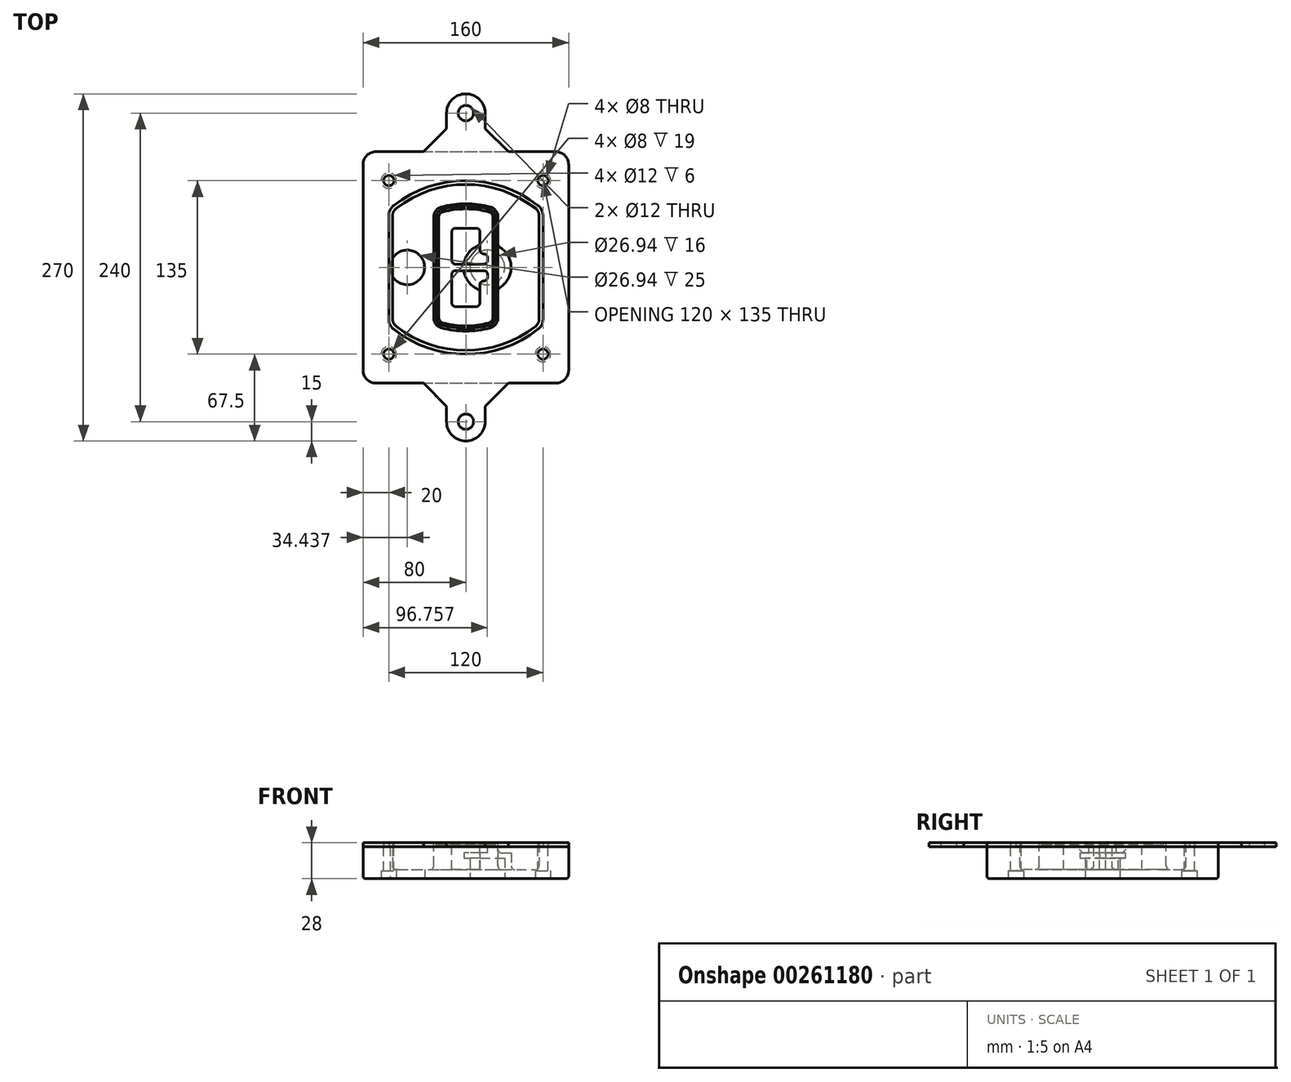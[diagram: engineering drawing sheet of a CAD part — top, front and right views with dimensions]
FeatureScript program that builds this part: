
annotation { "Feature Type Name" : "Feature", "Feature Type Description" : "" }
export const myFeature = defineFeature(function(context is Context, id is Id, definition is map)
    precondition{}
    {
        {
            var Q0;
            Q0=qCreatedBy(makeId("Top.planeOp"),FACE);
            var sketch = newSketch(context, id + "F0", { "sketchPlane" : qUnion([Q0])});
            skPoint(sketch, "E0.rect.middle", {"position": v(0, 0) * mm});
            skLineSegment(sketch, "E1.bottom", {"start": v(-70, -90) * mm, "end": v(70, -90) * mm});
            skLineSegment(sketch, "E1.top", {"start": v(-70, 90) * mm, "end": v(70, 90) * mm});
            skLineSegment(sketch, "E1.left", {"start": v(-80, -80) * mm, "end": v(-80, 80) * mm});
            skLineSegment(sketch, "E1.right", {"start": v(80, -80) * mm, "end": v(80, 80) * mm});
            skLineSegment(sketch, "E2", {"start": v(-80, 90) * mm, "end": v(80, -90) * mm, "construction": true});
            skLineSegment(sketch, "E3", {"start": v(80, 90) * mm, "end": v(-80, -90) * mm, "construction": true});
            skCircle(sketch, "E4", {"center": v(-60, 67.5) * mm, "radius": 4 * mm});
            skCircle(sketch, "E5", {"center": v(60, 67.5) * mm, "radius": 4 * mm});
            skCircle(sketch, "E6", {"center": v(60, -67.5) * mm, "radius": 4 * mm});
            skCircle(sketch, "E7", {"center": v(-60, -67.5) * mm, "radius": 4 * mm});
            skLineSegment(sketch, "E8", {"start": v(-60, 67.5) * mm, "end": v(60, 67.5) * mm, "construction": true});
            skLineSegment(sketch, "E9", {"start": v(60, 67.5) * mm, "end": v(60, -67.5) * mm, "construction": true});
            skLineSegment(sketch, "E10", {"start": v(60, -67.5) * mm, "end": v(-60, -67.5) * mm, "construction": true});
            skLineSegment(sketch, "E11", {"start": v(-60, -67.5) * mm, "end": v(-60, 67.5) * mm, "construction": true});
            skLineSegment(sketch, "E12", {"start": v(-60, 40.3) * mm, "end": v(-60, -40.3) * mm});
            skLineSegment(sketch, "E13", {"start": v(60, 40.3) * mm, "end": v(60, -40.3) * mm});
            skArc(sketch, "E14", {"start": v(56.15, 48.18) * mm, "mid": v(0, 67.5) * mm, "end": v(-56.15, 48.18) * mm});
            skArc(sketch, "E15", {"start": v(-56.15, -48.18) * mm, "mid": v(0, -67.5) * mm, "end": v(56.15, -48.18) * mm});
            skLineSegment(sketch, "E16", {"start": v(-60, 0) * mm, "end": v(60, 0) * mm, "construction": true});
            skPoint(sketch, "E17.visualSharp", {"position": v(-60, -45) * mm});
            skArc(sketch, "E17.filletArc", {"start": v(-60, -40.3) * mm, "mid": v(-58.99, -44.68) * mm, "end": v(-56.15, -48.18) * mm});
            skPoint(sketch, "E18.visualSharp", {"position": v(-60, 45) * mm});
            skArc(sketch, "E18.filletArc", {"start": v(-56.15, 48.18) * mm, "mid": v(-58.99, 44.68) * mm, "end": v(-60, 40.3) * mm});
            skPoint(sketch, "E19.visualSharp", {"position": v(60, 45) * mm});
            skArc(sketch, "E19.filletArc", {"start": v(60, 40.3) * mm, "mid": v(58.99, 44.68) * mm, "end": v(56.15, 48.18) * mm});
            skPoint(sketch, "E20.visualSharp", {"position": v(60, -45) * mm});
            skArc(sketch, "E20.filletArc", {"start": v(56.15, -48.18) * mm, "mid": v(58.99, -44.68) * mm, "end": v(60, -40.3) * mm});
            skPoint(sketch, "E21.visualSharp", {"position": v(-80, 90) * mm});
            skArc(sketch, "E21.filletArc", {"start": v(-70, 90) * mm, "mid": v(-77.07, 87.07) * mm, "end": v(-80, 80) * mm});
            skPoint(sketch, "E22.visualSharp", {"position": v(80, 90) * mm});
            skArc(sketch, "E22.filletArc", {"start": v(80, 80) * mm, "mid": v(77.07, 87.07) * mm, "end": v(70, 90) * mm});
            skPoint(sketch, "E23.visualSharp", {"position": v(80, -90) * mm});
            skArc(sketch, "E23.filletArc", {"start": v(70, -90) * mm, "mid": v(77.07, -87.07) * mm, "end": v(80, -80) * mm});
            skPoint(sketch, "E24.visualSharp", {"position": v(-80, -90) * mm});
            skArc(sketch, "E24.filletArc", {"start": v(-80, -80) * mm, "mid": v(-77.07, -87.07) * mm, "end": v(-70, -90) * mm});
            skArc(sketch, "E25.0", {"start": v(57, 40.3) * mm, "mid": v(56.3, 43.36) * mm, "end": v(54.3, 45.81) * mm});
            skLineSegment(sketch, "E25.1", {"start": v(57, 40.3) * mm, "end": v(57, -40.3) * mm});
            skArc(sketch, "E25.2", {"start": v(54.3, -45.81) * mm, "mid": v(56.3, -43.36) * mm, "end": v(57, -40.3) * mm});
            skArc(sketch, "E25.3", {"start": v(-54.3, -45.81) * mm, "mid": v(0, -64.5) * mm, "end": v(54.3, -45.81) * mm});
            skArc(sketch, "E25.4", {"start": v(-57, -40.3) * mm, "mid": v(-56.3, -43.36) * mm, "end": v(-54.3, -45.81) * mm});
            skArc(sketch, "E25.5", {"start": v(54.3, 45.81) * mm, "mid": v(0, 64.5) * mm, "end": v(-54.3, 45.81) * mm});
            skLineSegment(sketch, "E25.6", {"start": v(-57, 40.3) * mm, "end": v(-57, -40.3) * mm});
            skArc(sketch, "E25.7", {"start": v(-54.3, 45.81) * mm, "mid": v(-56.3, 43.36) * mm, "end": v(-57, 40.3) * mm});
            skArc(sketch, "E26.0", {"start": v(-58.62, 51.33) * mm, "mid": v(-62.58, 46.43) * mm, "end": v(-64, 40.3) * mm});
            skArc(sketch, "E26.1", {"start": v(58.62, 51.33) * mm, "mid": v(0, 71.5) * mm, "end": v(-58.62, 51.33) * mm});
            skArc(sketch, "E26.2", {"start": v(64, 40.3) * mm, "mid": v(62.58, 46.43) * mm, "end": v(58.62, 51.33) * mm});
            skLineSegment(sketch, "E26.3", {"start": v(64, 40.3) * mm, "end": v(64, -40.3) * mm});
            skArc(sketch, "E26.4", {"start": v(58.62, -51.33) * mm, "mid": v(62.58, -46.43) * mm, "end": v(64, -40.3) * mm});
            skLineSegment(sketch, "E26.5", {"start": v(-64, 40.3) * mm, "end": v(-64, -40.3) * mm});
            skArc(sketch, "E26.6", {"start": v(-58.62, -51.33) * mm, "mid": v(0, -71.5) * mm, "end": v(58.62, -51.33) * mm});
            skArc(sketch, "E26.7", {"start": v(-64, -40.3) * mm, "mid": v(-62.58, -46.43) * mm, "end": v(-58.62, -51.33) * mm});
            skSolve(sketch);
        }
        {
            var Q0;
            Q0=makeQuery(id+"F0.imprint","IMPRINT",FACE,{"disambiguationData":[TD([[makeQuery(id+"F0.imprint","IMPRINT",EDGE,{"derivedFrom":sQuery(id+"F0.wireOp",EDGE,"E1.bottom")}),1.0]])]});
            var Q1;
            Q1=makeQuery(id+"F0.imprint","IMPRINT",FACE,{"disambiguationData":[TD([[makeQuery(id+"F0.imprint","IMPRINT",EDGE,{"derivedFrom":sQuery(id+"F0.wireOp",EDGE,"E12")}),1.0]])]});
            var Q2;
            Q2=makeQuery(id+"F0.imprint","IMPRINT",FACE,{"disambiguationData":[TD([[makeQuery(id+"F0.imprint","IMPRINT",EDGE,{"derivedFrom":sQuery(id+"F0.wireOp",EDGE,"E25.0")}),1.0]])]});
            var Q3;
            Q3=makeQuery(id+"F0.imprint","IMPRINT",FACE,{"disambiguationData":[TD([[makeQuery(id+"F0.imprint","IMPRINT",EDGE,{"derivedFrom":sQuery(id+"F0.wireOp",EDGE,"E12")}),-1.0]])]});
            extrude(context, id + "F1", {"entities" : qUnion([Q0, Q1, Q2, Q3]), "oppositeDirection" : true, "depth" : 25 * mm});
        }
        {
            var Q0;
            Q0=makeQuery(id+"F0.imprint","IMPRINT",FACE,{"disambiguationData":[TD([[makeQuery(id+"F0.imprint","IMPRINT",EDGE,{"derivedFrom":sQuery(id+"F0.wireOp",EDGE,"E12")}),1.0]])]});
            extrude(context, id + "F2", {"entities" : qUnion([Q0]), "operationType" : NewBodyOperationType.ADD, "depth" : 3 * mm});
        }
        {
            var Q0;
            Q0=makeQuery(id+"F0.imprint","IMPRINT",FACE,{"disambiguationData":[TD([[makeQuery(id+"F0.imprint","IMPRINT",EDGE,{"derivedFrom":sQuery(id+"F0.wireOp",EDGE,"E25.0")}),1.0]])]});
            extrude(context, id + "F3", {"entities" : qUnion([Q0]), "operationType" : NewBodyOperationType.REMOVE, "oppositeDirection" : true, "depth" : 18 * mm});
        }
        {
            var Q0;
            Q0=makeQuery(id+"F2.opExtrude","CAP_FACE",FACE,{"disambiguationData":[OSD([sQuery(id+"F0.wireOp",EDGE,"E12"),sQuery(id+"F0.wireOp",EDGE,"E13"),sQuery(id+"F0.wireOp",EDGE,"E14"),sQuery(id+"F0.wireOp",EDGE,"E15"),sQuery(id+"F0.wireOp",EDGE,"E17.filletArc"),sQuery(id+"F0.wireOp",EDGE,"E18.filletArc"),sQuery(id+"F0.wireOp",EDGE,"E19.filletArc"),sQuery(id+"F0.wireOp",EDGE,"E20.filletArc"),sQuery(id+"F0.wireOp",EDGE,"E25.0"),sQuery(id+"F0.wireOp",EDGE,"E25.1"),sQuery(id+"F0.wireOp",EDGE,"E25.2"),sQuery(id+"F0.wireOp",EDGE,"E25.3"),sQuery(id+"F0.wireOp",EDGE,"E25.4"),sQuery(id+"F0.wireOp",EDGE,"E25.5"),sQuery(id+"F0.wireOp",EDGE,"E25.6"),sQuery(id+"F0.wireOp",EDGE,"E25.7")])],"isStart":false});
            var sketch = newSketch(context, id + "F4", { "sketchPlane" : qUnion([Q0])});
            skArc(sketch, "E27.0", {"start": v(-19.08, -46.97) * mm, "mid": v(0, -49.5) * mm, "end": v(19.08, -46.97) * mm});
            skArc(sketch, "E28.0", {"start": v(19.08, 46.97) * mm, "mid": v(0, 49.5) * mm, "end": v(-19.08, 46.97) * mm});
            skLineSegment(sketch, "E29", {"start": v(-25, 39.25) * mm, "end": v(-25, -39.25) * mm});
            skLineSegment(sketch, "E30", {"start": v(25, 39.25) * mm, "end": v(25, -39.25) * mm});
            skLineSegment(sketch, "E31", {"start": v(-25, 45.1) * mm, "end": v(25, 45.1) * mm, "construction": true});
            skLineSegment(sketch, "E32", {"start": v(-25, -45.1) * mm, "end": v(25, -45.1) * mm, "construction": true});
            skPoint(sketch, "E33.visualSharp", {"position": v(-25, 45.1) * mm});
            skArc(sketch, "E33.filletArc", {"start": v(-19.08, 46.97) * mm, "mid": v(-23.35, 44.11) * mm, "end": v(-25, 39.25) * mm});
            skPoint(sketch, "E34.visualSharp", {"position": v(25, 45.1) * mm});
            skArc(sketch, "E34.filletArc", {"start": v(25, 39.25) * mm, "mid": v(23.35, 44.11) * mm, "end": v(19.08, 46.97) * mm});
            skPoint(sketch, "E35.visualSharp", {"position": v(25, -45.1) * mm});
            skArc(sketch, "E35.filletArc", {"start": v(19.08, -46.97) * mm, "mid": v(23.35, -44.11) * mm, "end": v(25, -39.25) * mm});
            skPoint(sketch, "E36.visualSharp", {"position": v(-25, -45.1) * mm});
            skArc(sketch, "E36.filletArc", {"start": v(-25, -39.25) * mm, "mid": v(-23.35, -44.11) * mm, "end": v(-19.08, -46.97) * mm});
            skArc(sketch, "E37.0", {"start": v(54.3, 45.81) * mm, "mid": v(0, 64.5) * mm, "end": v(-54.3, 45.81) * mm});
            skArc(sketch, "E37.1", {"start": v(-54.3, 45.81) * mm, "mid": v(-56.3, 43.36) * mm, "end": v(-57, 40.3) * mm});
            skLineSegment(sketch, "E37.2", {"start": v(-57, 40.3) * mm, "end": v(-57, -40.3) * mm});
            skArc(sketch, "E37.3", {"start": v(-57, -40.3) * mm, "mid": v(-56.3, -43.36) * mm, "end": v(-54.3, -45.81) * mm});
            skArc(sketch, "E37.4", {"start": v(-54.3, -45.81) * mm, "mid": v(0, -64.5) * mm, "end": v(54.3, -45.81) * mm});
            skArc(sketch, "E37.5", {"start": v(54.3, -45.81) * mm, "mid": v(56.3, -43.36) * mm, "end": v(57, -40.3) * mm});
            skLineSegment(sketch, "E37.6", {"start": v(57, 40.3) * mm, "end": v(57, -40.3) * mm});
            skArc(sketch, "E37.7", {"start": v(57, 40.3) * mm, "mid": v(56.3, 43.36) * mm, "end": v(54.3, 45.81) * mm});
            skLineSegment(sketch, "E38.0", {"start": v(23, 39.25) * mm, "end": v(23, -39.25) * mm});
            skArc(sketch, "E38.1", {"start": v(18.56, -45.04) * mm, "mid": v(21.76, -42.9) * mm, "end": v(23, -39.25) * mm});
            skArc(sketch, "E38.2", {"start": v(-18.56, -45.04) * mm, "mid": v(0, -47.5) * mm, "end": v(18.56, -45.04) * mm});
            skArc(sketch, "E38.3", {"start": v(-23, -39.25) * mm, "mid": v(-21.76, -42.9) * mm, "end": v(-18.56, -45.04) * mm});
            skLineSegment(sketch, "E38.4", {"start": v(-23, 39.25) * mm, "end": v(-23, -39.25) * mm});
            skArc(sketch, "E38.5", {"start": v(23, 39.25) * mm, "mid": v(21.76, 42.9) * mm, "end": v(18.56, 45.04) * mm});
            skArc(sketch, "E38.6", {"start": v(-18.56, 45.04) * mm, "mid": v(-21.76, 42.9) * mm, "end": v(-23, 39.25) * mm});
            skArc(sketch, "E38.7", {"start": v(18.56, 45.04) * mm, "mid": v(0, 47.5) * mm, "end": v(-18.56, 45.04) * mm});
            skArc(sketch, "E39.0", {"start": v(21, 39.25) * mm, "mid": v(20.18, 41.68) * mm, "end": v(18.04, 43.1) * mm});
            skLineSegment(sketch, "E39.1", {"start": v(21, 39.25) * mm, "end": v(21, -39.25) * mm});
            skArc(sketch, "E39.2", {"start": v(18.04, -43.1) * mm, "mid": v(20.18, -41.68) * mm, "end": v(21, -39.25) * mm});
            skArc(sketch, "E39.3", {"start": v(-18.04, -43.1) * mm, "mid": v(0, -45.5) * mm, "end": v(18.04, -43.1) * mm});
            skArc(sketch, "E39.4", {"start": v(-21, -39.25) * mm, "mid": v(-20.18, -41.68) * mm, "end": v(-18.04, -43.1) * mm});
            skArc(sketch, "E39.5", {"start": v(18.04, 43.1) * mm, "mid": v(0, 45.5) * mm, "end": v(-18.04, 43.1) * mm});
            skLineSegment(sketch, "E39.6", {"start": v(-21, 39.25) * mm, "end": v(-21, -39.25) * mm});
            skArc(sketch, "E39.7", {"start": v(-18.04, 43.1) * mm, "mid": v(-20.18, 41.68) * mm, "end": v(-21, 39.25) * mm});
            skLineSegment(sketch, "E40", {"start": v(-25, 0) * mm, "end": v(25, 0) * mm, "construction": true});
            skLineSegment(sketch, "E41", {"start": v(-11, 5.5) * mm, "end": v(-11, 27.5) * mm});
            skLineSegment(sketch, "E42", {"start": v(-8, 30.5) * mm, "end": v(8, 30.5) * mm});
            skLineSegment(sketch, "E43", {"start": v(11, 27.5) * mm, "end": v(11, 13.5) * mm});
            skLineSegment(sketch, "E44", {"start": v(14, 10.5) * mm, "end": v(14, 10.5) * mm});
            skLineSegment(sketch, "E45", {"start": v(17, 7.5) * mm, "end": v(17, 5.5) * mm});
            skLineSegment(sketch, "E46", {"start": v(14, 2.5) * mm, "end": v(-8, 2.5) * mm});
            skPoint(sketch, "E47.visualSharp", {"position": v(-11, 30.5) * mm});
            skArc(sketch, "E47.filletArc", {"start": v(-8, 30.5) * mm, "mid": v(-10.12, 29.62) * mm, "end": v(-11, 27.5) * mm});
            skPoint(sketch, "E48.visualSharp", {"position": v(11, 30.5) * mm});
            skArc(sketch, "E48.filletArc", {"start": v(11, 27.5) * mm, "mid": v(10.12, 29.62) * mm, "end": v(8, 30.5) * mm});
            skPoint(sketch, "E49.visualSharp", {"position": v(11, 10.5) * mm});
            skArc(sketch, "E49.filletArc", {"start": v(11, 13.5) * mm, "mid": v(11.88, 11.38) * mm, "end": v(14, 10.5) * mm});
            skPoint(sketch, "E50.visualSharp", {"position": v(17, 10.5) * mm});
            skArc(sketch, "E50.filletArc", {"start": v(17, 7.5) * mm, "mid": v(16.12, 9.62) * mm, "end": v(14, 10.5) * mm});
            skPoint(sketch, "E51.visualSharp", {"position": v(17, 2.5) * mm});
            skArc(sketch, "E51.filletArc", {"start": v(14, 2.5) * mm, "mid": v(16.12, 3.38) * mm, "end": v(17, 5.5) * mm});
            skPoint(sketch, "E52.visualSharp", {"position": v(-11, 2.5) * mm});
            skArc(sketch, "E52.filletArc", {"start": v(-11, 5.5) * mm, "mid": v(-10.12, 3.38) * mm, "end": v(-8, 2.5) * mm});
            skLineSegment(sketch, "E53.0.MirrorCS", {"start": v(14, -2.5) * mm, "end": v(-8, -2.5) * mm});
            skArc(sketch, "E54.0.MirrorCS", {"start": v(-11, -5.5) * mm, "mid": v(-10.12, -3.38) * mm, "end": v(-8, -2.5) * mm});
            skLineSegment(sketch, "E55.0.MirrorCS", {"start": v(-11, -5.5) * mm, "end": v(-11, -27.5) * mm});
            skArc(sketch, "E56.0.MirrorCS", {"start": v(-8, -30.5) * mm, "mid": v(-10.12, -29.62) * mm, "end": v(-11, -27.5) * mm});
            skLineSegment(sketch, "E57.0.MirrorCS", {"start": v(-8, -30.5) * mm, "end": v(8, -30.5) * mm});
            skArc(sketch, "E58.0.MirrorCS", {"start": v(11, -27.5) * mm, "mid": v(10.12, -29.62) * mm, "end": v(8, -30.5) * mm});
            skLineSegment(sketch, "E59.0.MirrorCS", {"start": v(11, -27.5) * mm, "end": v(11, -13.5) * mm});
            skArc(sketch, "E60.0.MirrorCS", {"start": v(11, -13.5) * mm, "mid": v(11.88, -11.38) * mm, "end": v(14, -10.5) * mm});
            skArc(sketch, "E61.0.MirrorCS", {"start": v(17, -7.5) * mm, "mid": v(16.12, -9.62) * mm, "end": v(14, -10.5) * mm});
            skLineSegment(sketch, "E62.0.MirrorCS", {"start": v(17, -7.5) * mm, "end": v(17, -5.5) * mm});
            skArc(sketch, "E63.0.MirrorCS", {"start": v(14, -2.5) * mm, "mid": v(16.12, -3.38) * mm, "end": v(17, -5.5) * mm});
            skSolve(sketch);
        }
        {
            var Q0;
            Q0=makeQuery(id+"F4.imprint","IMPRINT",FACE,{"disambiguationData":[TD([[makeQuery(id+"F4.imprint","IMPRINT",EDGE,{"derivedFrom":sQuery(id+"F4.wireOp",EDGE,"E27.0")}),1.0]])]});
            var Q1;
            Q1=makeQuery(id+"F4.imprint","IMPRINT",FACE,{"disambiguationData":[TD([[makeQuery(id+"F4.imprint","IMPRINT",EDGE,{"derivedFrom":sQuery(id+"F4.wireOp",EDGE,"E38.0")}),-1.0]])]});
            var Q2;
            Q2=makeQuery(id+"F4.imprint","IMPRINT",FACE,{"disambiguationData":[TD([[makeQuery(id+"F4.imprint","IMPRINT",EDGE,{"derivedFrom":sQuery(id+"F4.wireOp",EDGE,"E39.0")}),1.0]])]});
            extrude(context, id + "F5", {"entities" : qUnion([Q0, Q1, Q2]), "operationType" : NewBodyOperationType.ADD, "endBound" : BoundingType.UP_TO_NEXT, "oppositeDirection" : true, "depth" : 25 * mm});
        }
        {
            var Q0;
            Q0=makeQuery(id+"F4.imprint","IMPRINT",FACE,{"disambiguationData":[TD([[makeQuery(id+"F4.imprint","IMPRINT",EDGE,{"derivedFrom":sQuery(id+"F4.wireOp",EDGE,"E38.0")}),-1.0]])]});
            extrude(context, id + "F6", {"entities" : qUnion([Q0]), "operationType" : NewBodyOperationType.REMOVE, "oppositeDirection" : true, "depth" : 2 * mm});
        }
        {
            var Q0;
            Q0=makeQuery(id+"F1.opExtrude","CAP_FACE",FACE,{"disambiguationData":[OSD([sQuery(id+"F0.wireOp",EDGE,"E1.bottom"),sQuery(id+"F0.wireOp",EDGE,"E1.top"),sQuery(id+"F0.wireOp",EDGE,"E1.left"),sQuery(id+"F0.wireOp",EDGE,"E1.right"),sQuery(id+"F0.wireOp",EDGE,"E4"),sQuery(id+"F0.wireOp",EDGE,"E5"),sQuery(id+"F0.wireOp",EDGE,"E6"),sQuery(id+"F0.wireOp",EDGE,"E7"),sQuery(id+"F0.wireOp",EDGE,"E21.filletArc"),sQuery(id+"F0.wireOp",EDGE,"E22.filletArc"),sQuery(id+"F0.wireOp",EDGE,"E23.filletArc"),sQuery(id+"F0.wireOp",EDGE,"E24.filletArc")])],"isStart":false});
            var sketch = newSketch(context, id + "F7", { "sketchPlane" : qUnion([Q0])});
            skCircle(sketch, "E64", {"center": v(16.76, 0) * mm, "radius": 13.47 * mm});
            skCircle(sketch, "E65", {"center": v(-45.56, 0) * mm, "radius": 13.47 * mm});
            skLineSegment(sketch, "E66", {"start": v(80, 0) * mm, "end": v(-80, 0) * mm});
            skCircle(sketch, "E67", {"center": v(16.76, 0) * mm, "radius": 18.47 * mm});
            skCircle(sketch, "E68", {"center": v(60, -67.5) * mm, "radius": 6 * mm});
            skCircle(sketch, "E69", {"center": v(-60, -67.5) * mm, "radius": 6 * mm});
            skCircle(sketch, "E70", {"center": v(-60, 67.5) * mm, "radius": 6 * mm});
            skCircle(sketch, "E71", {"center": v(60, 67.5) * mm, "radius": 6 * mm});
            skSolve(sketch);
        }
        {
            var Q0;
            {var subQ1=sQuery(id+"F7.wireOp",EDGE,"E66");var subQ4=sQuery(id+"F7.wireOp",EDGE,"E64");var subQ6=makeQuery(id+"F7.imprint","INTERSECT",VERTEX,{"disambiguationData":[OD(0.0)],"derivedFrom":[subQ4,subQ1]});Q0=makeQuery(id+"F7.imprint","IMPRINT",FACE,{"disambiguationData":[TD([[makeQuery(id+"F7.imprint","IMPRINT",EDGE,{"disambiguationData":[TD([[subQ6,-1.0]])],"derivedFrom":subQ4}),-1.0]])]});}
            var Q1;
            {var subQ0=sQuery(id+"F7.wireOp",EDGE,"E66");var subQ1=sQuery(id+"F7.wireOp",EDGE,"E64");var subQ3=makeQuery(id+"F7.imprint","INTERSECT",VERTEX,{"disambiguationData":[OD(0.0)],"derivedFrom":[subQ1,subQ0]});Q1=makeQuery(id+"F7.imprint","IMPRINT",FACE,{"disambiguationData":[TD([[makeQuery(id+"F7.imprint","IMPRINT",EDGE,{"disambiguationData":[TD([[subQ3,-1.0]])],"derivedFrom":subQ1}),1.0]])]});}
            var Q2;
            {var subQ0=sQuery(id+"F7.wireOp",EDGE,"E66");var subQ1=sQuery(id+"F7.wireOp",EDGE,"E64");var subQ3=makeQuery(id+"F7.imprint","INTERSECT",VERTEX,{"disambiguationData":[OD(0.0)],"derivedFrom":[subQ1,subQ0]});Q2=makeQuery(id+"F7.imprint","IMPRINT",FACE,{"disambiguationData":[TD([[makeQuery(id+"F7.imprint","IMPRINT",EDGE,{"disambiguationData":[TD([[subQ3,1.0]])],"derivedFrom":subQ1}),1.0]])]});}
            var Q3;
            {var subQ1=sQuery(id+"F7.wireOp",EDGE,"E66");var subQ4=sQuery(id+"F7.wireOp",EDGE,"E64");var subQ6=makeQuery(id+"F7.imprint","INTERSECT",VERTEX,{"disambiguationData":[OD(0.0)],"derivedFrom":[subQ4,subQ1]});Q3=makeQuery(id+"F7.imprint","IMPRINT",FACE,{"disambiguationData":[TD([[makeQuery(id+"F7.imprint","IMPRINT",EDGE,{"disambiguationData":[TD([[subQ6,1.0]])],"derivedFrom":subQ4}),-1.0]])]});}
            extrude(context, id + "F8", {"entities" : qUnion([Q0, Q1, Q2, Q3]), "operationType" : NewBodyOperationType.ADD, "oppositeDirection" : true, "depth" : 20 * mm});
        }
        {
            var Q0;
            {var subQ0=sQuery(id+"F7.wireOp",EDGE,"E66");var subQ1=sQuery(id+"F7.wireOp",EDGE,"E64");var subQ3=makeQuery(id+"F7.imprint","INTERSECT",VERTEX,{"disambiguationData":[OD(0.0)],"derivedFrom":[subQ1,subQ0]});Q0=makeQuery(id+"F7.imprint","IMPRINT",FACE,{"disambiguationData":[TD([[makeQuery(id+"F7.imprint","IMPRINT",EDGE,{"disambiguationData":[TD([[subQ3,-1.0]])],"derivedFrom":subQ1}),1.0]])]});}
            var Q1;
            {var subQ0=sQuery(id+"F7.wireOp",EDGE,"E66");var subQ1=sQuery(id+"F7.wireOp",EDGE,"E64");var subQ3=makeQuery(id+"F7.imprint","INTERSECT",VERTEX,{"disambiguationData":[OD(0.0)],"derivedFrom":[subQ1,subQ0]});Q1=makeQuery(id+"F7.imprint","IMPRINT",FACE,{"disambiguationData":[TD([[makeQuery(id+"F7.imprint","IMPRINT",EDGE,{"disambiguationData":[TD([[subQ3,1.0]])],"derivedFrom":subQ1}),1.0]])]});}
            extrude(context, id + "F9", {"entities" : qUnion([Q0, Q1]), "operationType" : NewBodyOperationType.REMOVE, "oppositeDirection" : true, "depth" : 16 * mm});
        }
        {
            var Q0;
            {var subQ0=sQuery(id+"F7.wireOp",EDGE,"E66");var subQ1=sQuery(id+"F7.wireOp",EDGE,"E65");var subQ3=makeQuery(id+"F7.imprint","INTERSECT",VERTEX,{"disambiguationData":[OD(0.0)],"derivedFrom":[subQ1,subQ0]});Q0=makeQuery(id+"F7.imprint","IMPRINT",FACE,{"disambiguationData":[TD([[makeQuery(id+"F7.imprint","IMPRINT",EDGE,{"disambiguationData":[TD([[subQ3,-1.0]])],"derivedFrom":subQ1}),1.0]])]});}
            var Q1;
            {var subQ0=sQuery(id+"F7.wireOp",EDGE,"E66");var subQ1=sQuery(id+"F7.wireOp",EDGE,"E65");var subQ3=makeQuery(id+"F7.imprint","INTERSECT",VERTEX,{"disambiguationData":[OD(0.0)],"derivedFrom":[subQ1,subQ0]});Q1=makeQuery(id+"F7.imprint","IMPRINT",FACE,{"disambiguationData":[TD([[makeQuery(id+"F7.imprint","IMPRINT",EDGE,{"disambiguationData":[TD([[subQ3,1.0]])],"derivedFrom":subQ1}),1.0]])]});}
            extrude(context, id + "F10", {"entities" : qUnion([Q0, Q1]), "operationType" : NewBodyOperationType.REMOVE, "oppositeDirection" : true, "depth" : 25 * mm});
        }
        {
            var Q0;
            Q0=makeQuery(id+"F7.imprint","IMPRINT",FACE,{"disambiguationData":[TD([[makeQuery(id+"F7.imprint","IMPRINT",EDGE,{"derivedFrom":sQuery(id+"F7.wireOp",EDGE,"E68")}),1.0]])]});
            var Q1;
            Q1=makeQuery(id+"F7.imprint","IMPRINT",FACE,{"disambiguationData":[TD([[makeQuery(id+"F7.imprint","IMPRINT",EDGE,{"derivedFrom":makeQuery(id+"F1.opExtrude","CAP_EDGE",EDGE,{"disambiguationData":[OSD([sQuery(id+"F0.wireOp",EDGE,"E5")])],"isStart":false})}),-1.0]])]});
            var Q2;
            Q2=makeQuery(id+"F7.imprint","IMPRINT",FACE,{"disambiguationData":[TD([[makeQuery(id+"F7.imprint","IMPRINT",EDGE,{"derivedFrom":sQuery(id+"F7.wireOp",EDGE,"E69")}),1.0]])]});
            var Q3;
            Q3=makeQuery(id+"F7.imprint","IMPRINT",FACE,{"disambiguationData":[TD([[makeQuery(id+"F7.imprint","IMPRINT",EDGE,{"derivedFrom":makeQuery(id+"F1.opExtrude","CAP_EDGE",EDGE,{"disambiguationData":[OSD([sQuery(id+"F0.wireOp",EDGE,"E4")])],"isStart":false})}),-1.0]])]});
            var Q4;
            Q4=makeQuery(id+"F7.imprint","IMPRINT",FACE,{"disambiguationData":[TD([[makeQuery(id+"F7.imprint","IMPRINT",EDGE,{"derivedFrom":sQuery(id+"F7.wireOp",EDGE,"E70")}),1.0]])]});
            var Q5;
            Q5=makeQuery(id+"F7.imprint","IMPRINT",FACE,{"disambiguationData":[TD([[makeQuery(id+"F7.imprint","IMPRINT",EDGE,{"derivedFrom":makeQuery(id+"F1.opExtrude","CAP_EDGE",EDGE,{"disambiguationData":[OSD([sQuery(id+"F0.wireOp",EDGE,"E7")])],"isStart":false})}),-1.0]])]});
            var Q6;
            Q6=makeQuery(id+"F7.imprint","IMPRINT",FACE,{"disambiguationData":[TD([[makeQuery(id+"F7.imprint","IMPRINT",EDGE,{"derivedFrom":sQuery(id+"F7.wireOp",EDGE,"E71")}),1.0]])]});
            var Q7;
            Q7=makeQuery(id+"F7.imprint","IMPRINT",FACE,{"disambiguationData":[TD([[makeQuery(id+"F7.imprint","IMPRINT",EDGE,{"derivedFrom":makeQuery(id+"F1.opExtrude","CAP_EDGE",EDGE,{"disambiguationData":[OSD([sQuery(id+"F0.wireOp",EDGE,"E6")])],"isStart":false})}),-1.0]])]});
            extrude(context, id + "F11", {"entities" : qUnion([Q0, Q1, Q2, Q3, Q4, Q5, Q6, Q7]), "operationType" : NewBodyOperationType.REMOVE, "oppositeDirection" : true, "depth" : 6 * mm});
        }
        {
            var Q0;
            Q0=makeQuery(id+"F9.boolean.opBoolean","COPY",FACE,{"derivedFrom":makeQuery(id+"F9.opExtrude","CAP_FACE",FACE,{"disambiguationData":[OSD([sQuery(id+"F7.wireOp",EDGE,"E64")])],"isStart":false})});
            var sketch = newSketch(context, id + "F12", { "sketchPlane" : qUnion([Q0])});
            skArc(sketch, "E72.0", {"start": v(11, 17.55) * mm, "mid": v(2.57, 11.82) * mm, "end": v(-1.54, 2.5) * mm});
            skArc(sketch, "E72.1", {"start": v(-1.54, -2.5) * mm, "mid": v(2.57, -11.82) * mm, "end": v(11, -17.55) * mm});
            skLineSegment(sketch, "E73", {"start": v(-1.54, -2.5) * mm, "end": v(14, -2.5) * mm});
            skLineSegment(sketch, "E74.0", {"start": v(14, 2.5) * mm, "end": v(-1.54, 2.5) * mm});
            skArc(sketch, "E74.1", {"start": v(14, 2.5) * mm, "mid": v(16.12, 3.38) * mm, "end": v(17, 5.5) * mm});
            skLineSegment(sketch, "E74.2", {"start": v(17, 7.5) * mm, "end": v(17, 5.5) * mm});
            skArc(sketch, "E74.3", {"start": v(17, 7.5) * mm, "mid": v(16.12, 9.62) * mm, "end": v(14, 10.5) * mm});
            skArc(sketch, "E74.4", {"start": v(11, 13.5) * mm, "mid": v(11.88, 11.38) * mm, "end": v(14, 10.5) * mm});
            skLineSegment(sketch, "E74.5", {"start": v(11, 17.55) * mm, "end": v(11, 13.5) * mm});
            skLineSegment(sketch, "E74.7", {"start": v(14, -2.5) * mm, "end": v(-1.54, -2.5) * mm});
            skArc(sketch, "E74.8", {"start": v(14, -2.5) * mm, "mid": v(16.12, -3.38) * mm, "end": v(17, -5.5) * mm});
            skLineSegment(sketch, "E74.9", {"start": v(17, -7.5) * mm, "end": v(17, -5.5) * mm});
            skArc(sketch, "E74.10", {"start": v(17, -7.5) * mm, "mid": v(16.12, -9.62) * mm, "end": v(14, -10.5) * mm});
            skArc(sketch, "E74.11", {"start": v(11, -13.5) * mm, "mid": v(11.88, -11.38) * mm, "end": v(14, -10.5) * mm});
            skLineSegment(sketch, "E74.12", {"start": v(11, -17.55) * mm, "end": v(11, -13.5) * mm});
            skPoint(sketch, "E75.orphan", {"position": v(11, -27.5) * mm});
            skPoint(sketch, "E76.orphan", {"position": v(-8, -2.5) * mm});
            skPoint(sketch, "E77.orphan", {"position": v(-8, 2.5) * mm});
            skPoint(sketch, "E78.orphan", {"position": v(11, 27.5) * mm});
            skSolve(sketch);
        }
        {
            var Q0;
            {var subQ7=sQuery(id+"F12.wireOp",EDGE,"E72.0");var subQ14=sQuery(id+"F12.wireOp",EDGE,"E72.1");var subQ16=sQuery(id+"F12.wireOp",EDGE,"E74.1");var subQ18=sQuery(id+"F12.wireOp",EDGE,"E74.8");Q0=qUnion([makeQuery(id+"F12.imprint","IMPRINT",FACE,{"disambiguationData":[TD([[makeQuery(id+"F12.imprint","IMPRINT",EDGE,{"derivedFrom":subQ7}),1.0]])]}),makeQuery(id+"F12.imprint","IMPRINT",FACE,{"disambiguationData":[TD([[makeQuery(id+"F12.imprint","IMPRINT",EDGE,{"derivedFrom":subQ14}),1.0]])]}),makeQuery(id+"F12.imprint","IMPRINT",FACE,{"disambiguationData":[TD([[makeQuery(id+"F12.imprint","IMPRINT",EDGE,{"derivedFrom":subQ16}),1.0]])]}),makeQuery(id+"F12.imprint","IMPRINT",FACE,{"disambiguationData":[TD([[makeQuery(id+"F12.imprint","IMPRINT",EDGE,{"derivedFrom":subQ18}),-1.0]])]})]);}
            var Q1;
            Q1=makeQuery(id+"F5.boolean.opBoolean","SPLIT",FACE,{"disambiguationData":[TD([makeQuery(id+"F5.opExtrude","SWEPT_FACE",FACE,{"disambiguationData":[OSD([sQuery(id+"F4.wireOp",EDGE,"E41")])]})])],"derivedFrom":makeQuery(id+"F3.boolean.opBoolean","COPY",FACE,{"derivedFrom":makeQuery(id+"F3.opExtrude","CAP_FACE",FACE,{"disambiguationData":[OSD([sQuery(id+"F0.wireOp",EDGE,"E25.0"),sQuery(id+"F0.wireOp",EDGE,"E25.1"),sQuery(id+"F0.wireOp",EDGE,"E25.2"),sQuery(id+"F0.wireOp",EDGE,"E25.3"),sQuery(id+"F0.wireOp",EDGE,"E25.4"),sQuery(id+"F0.wireOp",EDGE,"E25.5"),sQuery(id+"F0.wireOp",EDGE,"E25.6"),sQuery(id+"F0.wireOp",EDGE,"E25.7")])],"isStart":false})})});
            extrude(context, id + "F13", {"entities" : qUnion([Q0]), "operationType" : NewBodyOperationType.REMOVE, "endBound" : BoundingType.UP_TO_SURFACE, "endBoundEntityFace" : qUnion([Q1]), "depth" : 25 * mm});
        }
        {
            var Q0;
            Q0=makeQuery(id+"F3.boolean.opBoolean","COPY",EDGE,{"derivedFrom":makeQuery(id+"F3.opExtrude","CAP_EDGE",EDGE,{"disambiguationData":[OSD([sQuery(id+"F0.wireOp",EDGE,"E25.6")])],"isStart":false})});
            var Q1;
            Q1=makeQuery(id+"F8.boolean.opBoolean","INTERSECT",EDGE,{"derivedFrom":[makeQuery(id+"F5.opExtrude","SWEPT_FACE",FACE,{"disambiguationData":[OSD([sQuery(id+"F4.wireOp",EDGE,"E30")])]}),makeQuery(id+"F8.opExtrude","CAP_FACE",FACE,{"disambiguationData":[OSD([sQuery(id+"F7.wireOp",EDGE,"E67")])],"isStart":false})]});
            var Q2;
            Q2=makeQuery(id+"F8.boolean.opBoolean","INTERSECT",EDGE,{"disambiguationData":[OD(1.0)],"derivedFrom":[makeQuery(id+"F5.opExtrude","SWEPT_FACE",FACE,{"disambiguationData":[OSD([sQuery(id+"F4.wireOp",EDGE,"E30")])]}),makeQuery(id+"F8.opExtrude","SWEPT_FACE",FACE,{"disambiguationData":[OSD([sQuery(id+"F7.wireOp",EDGE,"E67")])]})]});
            var Q3;
            {var subQ0=sQuery(id+"F4.wireOp",EDGE,"E30");Q3=makeQuery(id+"F8.boolean.opBoolean","SPLIT",EDGE,{"disambiguationData":[TD([makeQuery(id+"F5.opExtrude","SWEPT_FACE",FACE,{"disambiguationData":[OSD([sQuery(id+"F4.wireOp",EDGE,"E35.filletArc")])]})])],"derivedFrom":makeQuery(id+"F5.opExtrude","CAP_EDGE",EDGE,{"disambiguationData":[OSD([subQ0])],"isStart":false})});}
            var Q4;
            {var subQ0=sQuery(id+"F0.wireOp",EDGE,"E25.7");var subQ1=sQuery(id+"F0.wireOp",EDGE,"E25.1");var subQ2=sQuery(id+"F0.wireOp",EDGE,"E25.6");var subQ3=sQuery(id+"F0.wireOp",EDGE,"E25.5");var subQ4=sQuery(id+"F0.wireOp",EDGE,"E25.4");var subQ5=sQuery(id+"F0.wireOp",EDGE,"E25.0");var subQ6=sQuery(id+"F0.wireOp",EDGE,"E25.2");var subQ7=sQuery(id+"F0.wireOp",EDGE,"E25.3");Q4=makeQuery(id+"F8.boolean.opBoolean","INTERSECT",EDGE,{"derivedFrom":[makeQuery(id+"F5.boolean.opBoolean","SPLIT",FACE,{"disambiguationData":[TD([makeQuery(id+"F2.opExtrude","SWEPT_FACE",FACE,{"disambiguationData":[OSD([subQ5])]})])],"derivedFrom":makeQuery(id+"F3.boolean.opBoolean","COPY",FACE,{"derivedFrom":makeQuery(id+"F3.opExtrude","CAP_FACE",FACE,{"disambiguationData":[OSD([subQ5,subQ1,subQ6,subQ7,subQ4,subQ3,subQ2,subQ0])],"isStart":false})})}),makeQuery(id+"F8.opExtrude","SWEPT_FACE",FACE,{"disambiguationData":[OSD([sQuery(id+"F7.wireOp",EDGE,"E67")])]})]});}
            var Q5;
            Q5=makeQuery(id+"F8.boolean.opBoolean","INTERSECT",EDGE,{"disambiguationData":[OD(0.0)],"derivedFrom":[makeQuery(id+"F5.opExtrude","SWEPT_FACE",FACE,{"disambiguationData":[OSD([sQuery(id+"F4.wireOp",EDGE,"E30")])]}),makeQuery(id+"F8.opExtrude","SWEPT_FACE",FACE,{"disambiguationData":[OSD([sQuery(id+"F7.wireOp",EDGE,"E67")])]})]});
            fillet(context, id + "F14", {"entities" : qUnion([Q0, Q1, Q2, Q3, Q4, Q5]), "radius" : 3 * mm, "tangentPropagation" : true, "allowEdgeOverflow" : false});
        }
        {
            var Q0;
            Q0=makeQuery(id+"F1.opExtrude","CAP_EDGE",EDGE,{"disambiguationData":[OSD([sQuery(id+"F0.wireOp",EDGE,"E1.bottom")])],"isStart":false});
            fillet(context, id + "F15", {"entities" : qUnion([Q0]), "radius" : 2 * mm, "tangentPropagation" : true, "allowEdgeOverflow" : false});
        }
        {
            var Q0;
            {var subQ0=sQuery(id+"F0.wireOp",EDGE,"E22.filletArc");var subQ1=sQuery(id+"F0.wireOp",EDGE,"E7");var subQ2=sQuery(id+"F0.wireOp",EDGE,"E6");var subQ3=sQuery(id+"F0.wireOp",EDGE,"E5");var subQ4=sQuery(id+"F0.wireOp",EDGE,"E4");var subQ5=sQuery(id+"F0.wireOp",EDGE,"E1.bottom");var subQ6=sQuery(id+"F0.wireOp",EDGE,"E21.filletArc");var subQ7=sQuery(id+"F0.wireOp",EDGE,"E1.top");var subQ8=sQuery(id+"F0.wireOp",EDGE,"E1.left");var subQ9=sQuery(id+"F0.wireOp",EDGE,"E1.right");var subQ10=sQuery(id+"F0.wireOp",EDGE,"E23.filletArc");var subQ11=sQuery(id+"F0.wireOp",EDGE,"E24.filletArc");Q0=makeQuery(id+"F2.boolean.opBoolean","SPLIT",FACE,{"disambiguationData":[TD([makeQuery(id+"F1.opExtrude","SWEPT_FACE",FACE,{"disambiguationData":[OSD([subQ5])]})])],"derivedFrom":makeQuery(id+"F1.opExtrude","CAP_FACE",FACE,{"disambiguationData":[OSD([subQ5,subQ7,subQ8,subQ9,subQ4,subQ3,subQ2,subQ1,subQ6,subQ0,subQ10,subQ11])],"isStart":true})});}
            var sketch = newSketch(context, id + "F16", { "sketchPlane" : qUnion([Q0])});
            skLineSegment(sketch, "E79", {"start": v(0, 90) * mm, "end": v(0, 120) * mm, "construction": true});
            skPoint(sketch, "E79.endSnap0", {"position": v(0, 90) * mm});
            skCircle(sketch, "E80", {"center": v(0, 120) * mm, "radius": 6 * mm});
            skLineSegment(sketch, "E81", {"start": v(0, 120) * mm, "end": v(15, 120) * mm, "construction": true});
            skArc(sketch, "E82", {"start": v(15, 120) * mm, "mid": v(0, 135) * mm, "end": v(-15, 120) * mm});
            skLineSegment(sketch, "E83", {"start": v(-15, 120) * mm, "end": v(-15, 108) * mm});
            skLineSegment(sketch, "E84", {"start": v(15, 120) * mm, "end": v(15, 108) * mm});
            skLineSegment(sketch, "E85", {"start": v(15, 108) * mm, "end": v(-15, 108) * mm, "construction": true});
            skPoint(sketch, "E86", {"position": v(0, 135) * mm});
            skLineSegment(sketch, "E87", {"start": v(-15, 108) * mm, "end": v(-15, 90) * mm, "construction": true});
            skLineSegment(sketch, "E88", {"start": v(-15, 90) * mm, "end": v(-33, 90) * mm});
            skLineSegment(sketch, "E89", {"start": v(-15, 108) * mm, "end": v(-33, 90) * mm});
            skLineSegment(sketch, "E90", {"start": v(15, 108) * mm, "end": v(15, 90) * mm, "construction": true});
            skLineSegment(sketch, "E91", {"start": v(15, 90) * mm, "end": v(33, 90) * mm, "construction": true});
            skLineSegment(sketch, "E92", {"start": v(15, 108) * mm, "end": v(33, 90) * mm});
            skLineSegment(sketch, "E93", {"start": v(-15, 90) * mm, "end": v(15, 90) * mm});
            skLineSegment(sketch, "E94", {"start": v(-80, 0) * mm, "end": v(80, 0) * mm, "construction": true});
            skLineSegment(sketch, "E95.MirrorCS", {"start": v(15, -120) * mm, "end": v(15, -108) * mm});
            skLineSegment(sketch, "E96.MirrorCS", {"start": v(-15, -120) * mm, "end": v(-15, -108) * mm});
            skLineSegment(sketch, "E97.MirrorCS", {"start": v(0, -90) * mm, "end": v(0, -120) * mm, "construction": true});
            skCircle(sketch, "E98.MirrorC", {"center": v(0, -120) * mm, "radius": 6 * mm});
            skLineSegment(sketch, "E99.MirrorCS", {"start": v(0, -120) * mm, "end": v(15, -120) * mm, "construction": true});
            skArc(sketch, "E100.MirrorCS", {"start": v(15, -120) * mm, "mid": v(0, -135) * mm, "end": v(-15, -120) * mm});
            skLineSegment(sketch, "E101.MirrorCS", {"start": v(15, -108) * mm, "end": v(-15, -108) * mm, "construction": true});
            skLineSegment(sketch, "E102.MirrorCS", {"start": v(15, -108) * mm, "end": v(15, -90) * mm, "construction": true});
            skPoint(sketch, "E103.MirrorP", {"position": v(0, -90) * mm});
            skPoint(sketch, "E104.MirrorP", {"position": v(0, -135) * mm});
            skLineSegment(sketch, "E105.MirrorCS", {"start": v(15, -108) * mm, "end": v(33, -90) * mm});
            skLineSegment(sketch, "E106.MirrorCS", {"start": v(-15, -108) * mm, "end": v(-15, -90) * mm, "construction": true});
            skLineSegment(sketch, "E107.MirrorCS", {"start": v(-15, -108) * mm, "end": v(-33, -90) * mm});
            skLineSegment(sketch, "E108", {"start": v(-33, -90) * mm, "end": v(33, -90) * mm});
            skSolve(sketch);
        }
        {
            var Q0;
            Q0=makeQuery(id+"F16.imprint","IMPRINT",FACE,{"disambiguationData":[TD([[makeQuery(id+"F16.imprint","IMPRINT",EDGE,{"derivedFrom":sQuery(id+"F16.wireOp",EDGE,"E80")}),-1.0]])]});
            var Q1;
            {var subQ7=sQuery(id+"F16.wireOp",EDGE,"E88");Q1=makeQuery(id+"F16.imprint","IMPRINT",FACE,{"disambiguationData":[TD([[makeQuery(id+"F16.imprint","IMPRINT",EDGE,{"derivedFrom":subQ7}),-1.0]])]});}
            var Q2;
            Q2=makeQuery(id+"F16.imprint","IMPRINT",FACE,{"disambiguationData":[TD([[makeQuery(id+"F16.imprint","IMPRINT",EDGE,{"derivedFrom":sQuery(id+"F16.wireOp",EDGE,"E95.MirrorCS")}),1.0]])]});
            var Q3;
            Q3=makeQuery(id+"F2.opExtrude","CAP_FACE",FACE,{"disambiguationData":[OSD([sQuery(id+"F0.wireOp",EDGE,"E12"),sQuery(id+"F0.wireOp",EDGE,"E13"),sQuery(id+"F0.wireOp",EDGE,"E14"),sQuery(id+"F0.wireOp",EDGE,"E15"),sQuery(id+"F0.wireOp",EDGE,"E17.filletArc"),sQuery(id+"F0.wireOp",EDGE,"E18.filletArc"),sQuery(id+"F0.wireOp",EDGE,"E19.filletArc"),sQuery(id+"F0.wireOp",EDGE,"E20.filletArc"),sQuery(id+"F0.wireOp",EDGE,"E25.0"),sQuery(id+"F0.wireOp",EDGE,"E25.1"),sQuery(id+"F0.wireOp",EDGE,"E25.2"),sQuery(id+"F0.wireOp",EDGE,"E25.3"),sQuery(id+"F0.wireOp",EDGE,"E25.4"),sQuery(id+"F0.wireOp",EDGE,"E25.5"),sQuery(id+"F0.wireOp",EDGE,"E25.6"),sQuery(id+"F0.wireOp",EDGE,"E25.7")])],"isStart":false});
            extrude(context, id + "F17", {"entities" : qUnion([Q0, Q1, Q2]), "endBound" : BoundingType.UP_TO_SURFACE, "endBoundEntityFace" : qUnion([Q3]), "depth" : 25 * mm});
        }
    });
